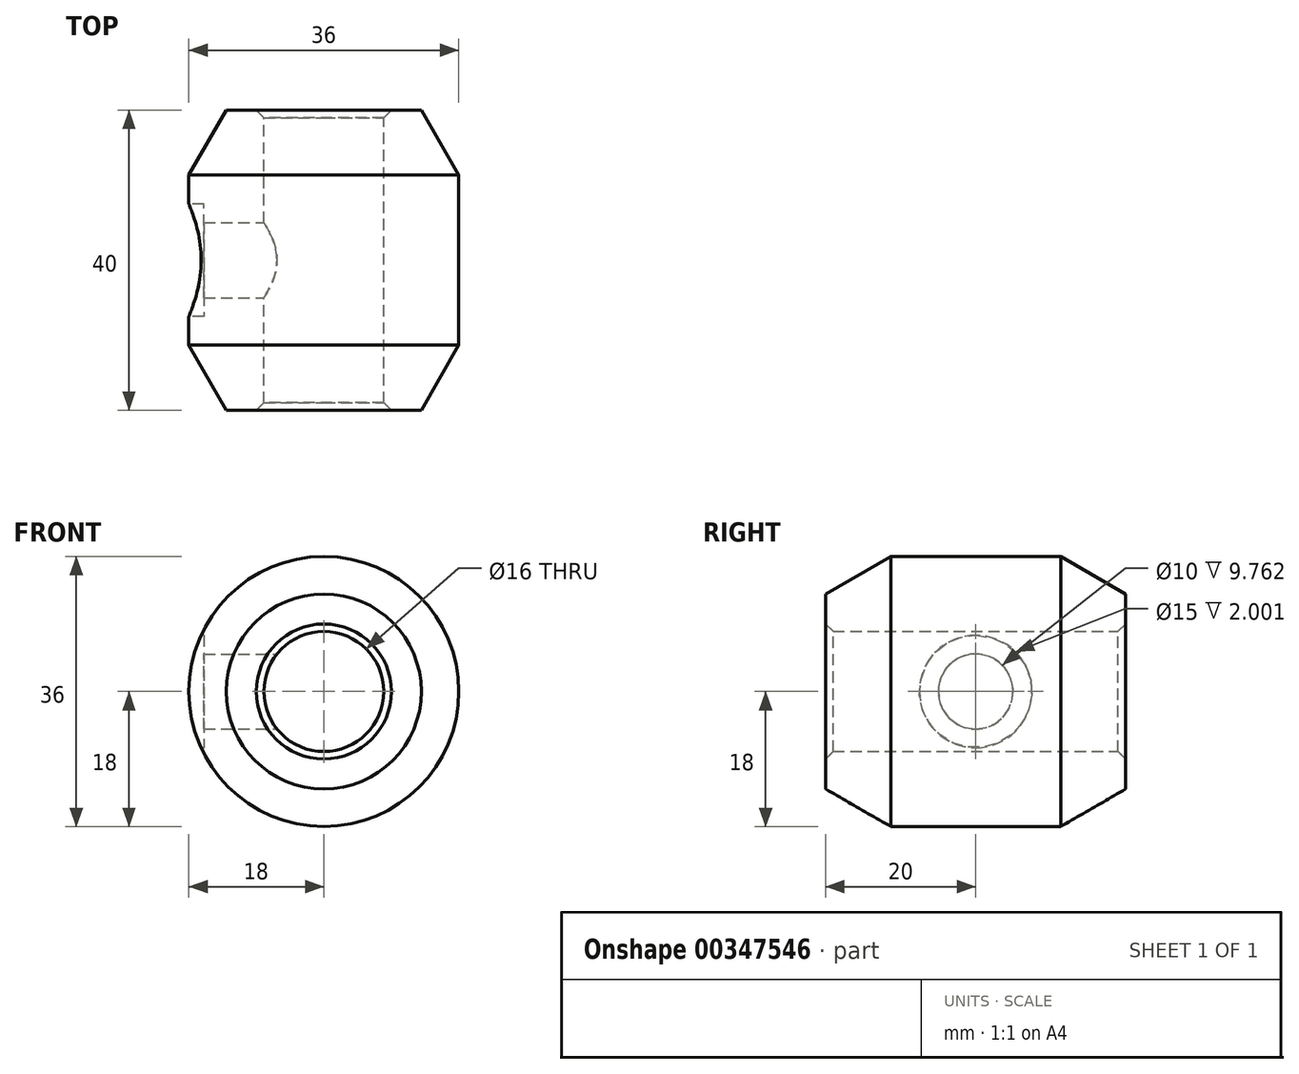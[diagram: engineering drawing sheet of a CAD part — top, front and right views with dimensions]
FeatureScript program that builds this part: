
annotation { "Feature Type Name" : "Feature", "Feature Type Description" : "" }
export const myFeature = defineFeature(function(context is Context, id is Id, definition is map)
    precondition{}
    {
        {
            var Q0;
            Q0=qCreatedBy(makeId("Front.planeOp"),FACE);
            var sketch = newSketch(context, id + "F0", { "sketchPlane" : qUnion([Q0])});
            skCircle(sketch, "E0", {"center": v(0, 0) * mm, "radius": 8 * mm});
            skCircle(sketch, "E1", {"center": v(0, 0) * mm, "radius": 18 * mm});
            skSolve(sketch);
        }
        {
            var Q0;
            Q0=makeQuery(id+"F0.imprint","IMPRINT",FACE,{"disambiguationData":[TD([[makeQuery(id+"F0.imprint","IMPRINT",EDGE,{"derivedFrom":sQuery(id+"F0.wireOp",EDGE,"E0")}),-1.0]])]});
            extrude(context, id + "F1", {"entities" : qUnion([Q0]), "depth" : 40 * mm});
        }
        {
            var Q0;
            Q0=qCreatedBy(makeId("Right.planeOp"),FACE);
            var sketch = newSketch(context, id + "F2", { "sketchPlane" : qUnion([Q0])});
            skLineSegment(sketch, "E2", {"start": v(-20, 24.04) * mm, "end": v(-20, -27.17) * mm, "construction": true});
            skLineSegment(sketch, "E3", {"start": v(-39, 0) * mm, "end": v(-1, 0) * mm, "construction": true});
            skCircle(sketch, "E4", {"center": v(-20, 0) * mm, "radius": 5 * mm});
            skLineSegment(sketch, "E5.0", {"start": v(-40, -18) * mm, "end": v(-40, 18) * mm, "construction": true});
            skLineSegment(sketch, "E6", {"start": v(0, -18) * mm, "end": v(-40, -18) * mm, "construction": true});
            skLineSegment(sketch, "E7", {"start": v(-40, 18) * mm, "end": v(0, 18) * mm, "construction": true});
            skSolve(sketch);
        }
        {
            var Q0;
            Q0=makeQuery(id+"F2.imprint","IMPRINT",FACE,{"disambiguationData":[TD([[makeQuery(id+"F2.imprint","IMPRINT",EDGE,{"derivedFrom":sQuery(id+"F2.wireOp",EDGE,"E4")}),1.0]])]});
            extrude(context, id + "F3", {"entities" : qUnion([Q0]), "operationType" : NewBodyOperationType.REMOVE, "oppositeDirection" : true, "depth" : 25 * mm});
        }
        {
            var Q0;
            Q0=qCreatedBy(makeId("Right.planeOp"),FACE);
            cPlane(context, id + "F4", {"entities" : qUnion([Q0]), "cplaneType" : CPlaneType.OFFSET, "offset" : (36 / 2) * mm, "oppositeDirection" : true, "width" : 150 * mm, "height" : 150 * mm});
        }
        {
            var Q0;
            Q0=qCreatedBy(id+"F4.planeOp",FACE);
            var sketch = newSketch(context, id + "F5", { "sketchPlane" : qUnion([Q0])});
            skCircle(sketch, "E8", {"center": v(-20, 0) * mm, "radius": 7.5 * mm});
            skSolve(sketch);
        }
        {
            var Q0;
            Q0=makeQuery(id+"F5.imprint","IMPRINT",FACE,{"disambiguationData":[TD([[makeQuery(id+"F5.imprint","IMPRINT",EDGE,{"derivedFrom":sQuery(id+"F5.wireOp",EDGE,"E8")}),1.0]])]});
            extrude(context, id + "F6", {"entities" : qUnion([Q0]), "operationType" : NewBodyOperationType.REMOVE, "depth" : 2 * mm});
        }
        {
            var Q0;
            Q0=makeQuery(id+"F1.opExtrude","CAP_EDGE",EDGE,{"disambiguationData":[OSD([sQuery(id+"F0.wireOp",EDGE,"E0")])],"isStart":false});
            var Q1;
            Q1=makeQuery(id+"F1.opExtrude","CAP_EDGE",EDGE,{"disambiguationData":[OSD([sQuery(id+"F0.wireOp",EDGE,"E0")])],"isStart":true});
            chamfer(context, id + "F7", {"entities" : qUnion([Q0, Q1]), "width" : 1 * mm, "tangentPropagation" : true});
        }
        {
            var Q0;
            Q0=makeQuery(id+"F1.opExtrude","CAP_EDGE",EDGE,{"disambiguationData":[OSD([sQuery(id+"F0.wireOp",EDGE,"E1")])],"isStart":false});
            var Q1;
            Q1=makeQuery(id+"F1.opExtrude","CAP_EDGE",EDGE,{"disambiguationData":[OSD([sQuery(id+"F0.wireOp",EDGE,"E1")])],"isStart":true});
            chamfer(context, id + "F8", {"entities" : qUnion([Q0, Q1]), "chamferType" : ChamferType.OFFSET_ANGLE, "width" : 5 * mm, "oppositeDirection" : false, "angle" : 60 * degree, "tangentPropagation" : true});
        }
    });
